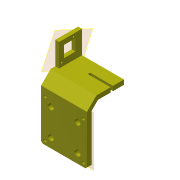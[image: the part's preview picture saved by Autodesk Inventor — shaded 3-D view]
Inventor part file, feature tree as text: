
AUTODESK INVENTOR PART (.ipt)
format: ipt  version: 2022 (Build 260153000, 153)  size: 176,128 bytes
history: native  units: mm
features: other x12, reference x12, sketch x6, extrude x4, plane x3, hole x2
ambient origin geometry x8: Origin, YZ Plane, XZ Plane, XY Plane, X Axis, Y Axis, Z Axis, Center Point
bodies: Solid1 (feature_tree)
feature tree (39):
  plane  "Work Plane1"
  plane  "Work Plane2"
  extrude  "Extrusion1"  Depth=5.0mm
  hole  "Hole1"  [1 undecoded]
  hole  "Hole3"  [1 undecoded]
  sketch  "Skizze13"  dims[d44=135.0deg d45=135.0deg]
  other  "Arbeitspunkt2"
  other  "Arbeitspunkt3"
  extrude  "Extrusion10"  Depth=30.0mm
  plane  "Arbeitsebene4"
  extrude  "Extrusion11"  Depth=30.0mm
  extrude  "Extrusion12"  Depth=15.0mm
  sketch  "Sketch1"  dims[d0=10.0mm d1=0.0mm]
  reference  "Reference1"
  reference  "Reference4"
  reference  "Reference5"
  sketch  "Sketch2"  dims[d2=4.0mm d3=6.0mm d4=8.0mm d5=4.5mm d6=90.0deg d7=8.0mm d8=20.594885mm]
  reference  "Reference6"
  reference  "Reference7"
  reference  "Reference8"
  reference  "Reference9"
  sketch  "Sketch10"  dims[d30=3.8mm d31=6.0mm d32=8.0mm d33=2.0mm d34=90.0deg d35=20.0mm d36=20.594885mm d43=5.0mm]
  reference  "Reference18"
  reference  "Reference19"
  reference  "Reference20"
  reference  "Reference21"
  reference  "Reference22"
  sketch  "Skizze14"  dims[d46=0.0mm d47=10.0mm d48=0.0mm]
  sketch  "Skizze15"  dims[d49=6.0mm d50=30.0mm d51=30.0mm d52=15.0mm d53=15.0mm d54=5.0mm d55=0.0mm d56=3.2mm d57=0.0mm d58=0.0mm]
  other  "<userpath>\Downloads\cellSTORM\cellSTORM_v5.iam"
  other  "cellSTORM_v5.iam"
  other  "00_XY_stage-CHUO_SEIKI_LD-647-R1:2"
  other  "00_XY_stage-CHUO_SEIKI_LD-647-R1-Bottom:1"
  other  "00_KES400:1"
  other  "00_KES400_Bluray_Lens:1"
  other  "00_XY_stage-CHUO_SEIKI_LD-647-R1:1"
  other  "00_XY_stage-CHUO_SEIKI_LD-647-R1-Top:1"
  other  "<userpath>\Documents\GitHub\cellstorm\INVENTOR\cellSTORM_v6.iam"
  other  "cellSTORM_v6.iam"
note: 2 required parameter values undecoded (feature->parameter linkage not recoverable at this tier; creation-order binding heuristic only, values carry confidence <= 0.55)
